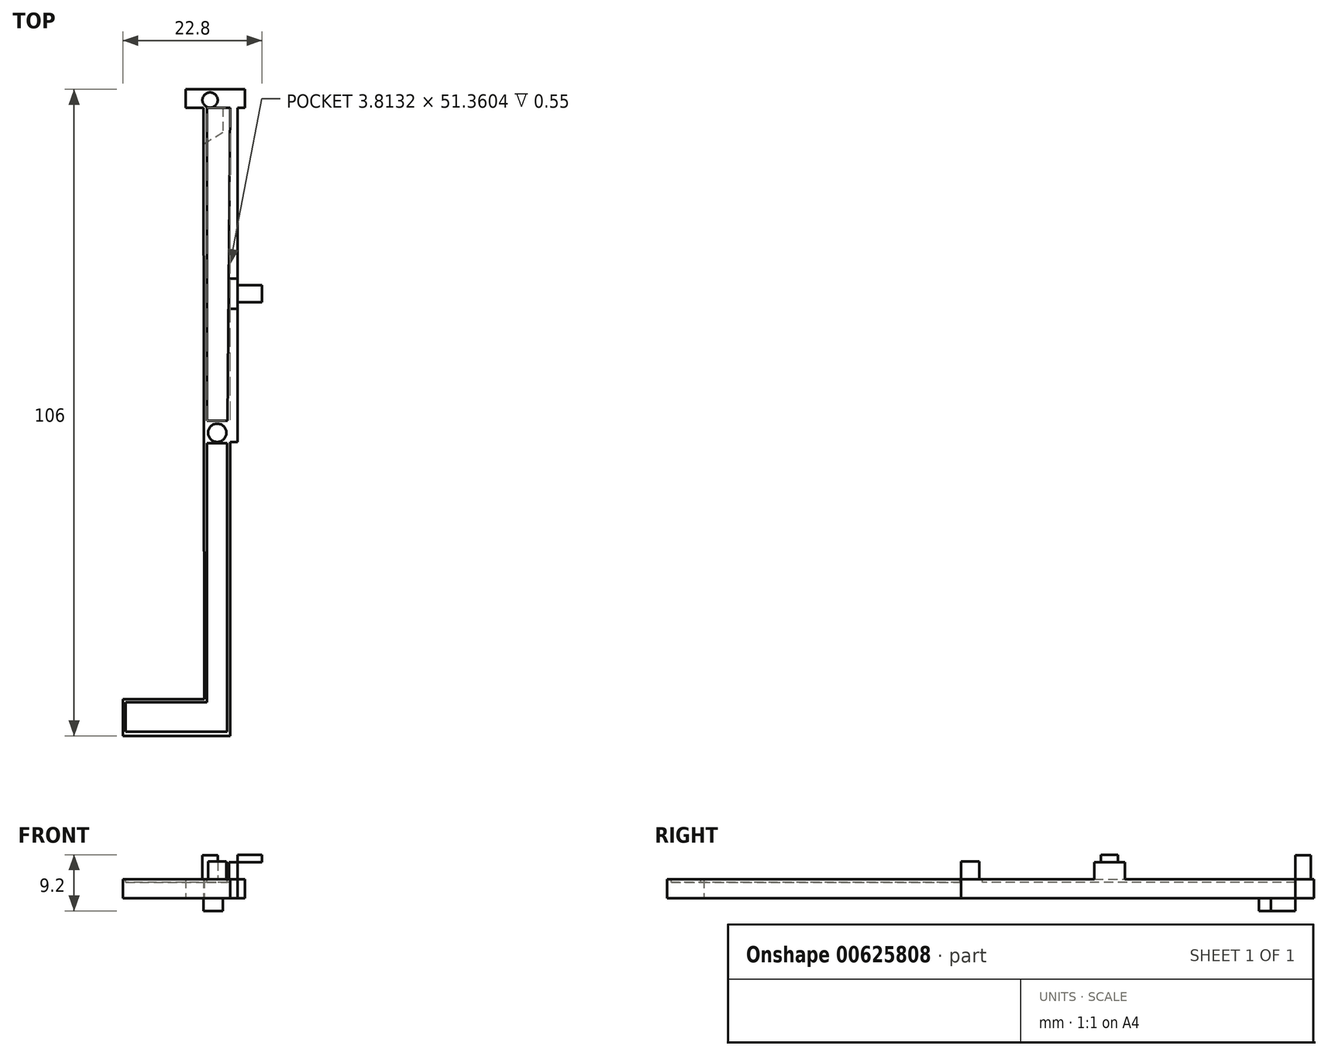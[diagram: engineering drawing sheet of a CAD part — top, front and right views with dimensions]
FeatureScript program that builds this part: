
annotation { "Feature Type Name" : "Feature", "Feature Type Description" : "" }
export const myFeature = defineFeature(function(context is Context, id is Id, definition is map)
    precondition{}
    {
        {
            var Q0;
            Q0=qCreatedBy(makeId("Top.planeOp"),FACE);
            var sketch = newSketch(context, id + "F0", { "sketchPlane" : qUnion([Q0])});
            skLineSegment(sketch, "E0", {"start": v(0, 3) * mm, "end": v(0, 0) * mm});
            skLineSegment(sketch, "E1", {"start": v(0, 0) * mm, "end": v(-1.2, 0) * mm});
            skLineSegment(sketch, "E2", {"start": v(0, 3) * mm, "end": v(-9.7, 3) * mm});
            skLineSegment(sketch, "E3", {"start": v(-9.7, 3) * mm, "end": v(-9.7, 0) * mm});
            skLineSegment(sketch, "E4", {"start": v(-9.7, 0) * mm, "end": v(-6.8, 0) * mm});
            skLineSegment(sketch, "E5", {"start": v(-1.2, 0) * mm, "end": v(-1.2, -54.8) * mm});
            skLineSegment(sketch, "E6", {"start": v(-1.2, -54.8) * mm, "end": v(-2.4, -54.8) * mm});
            skLineSegment(sketch, "E7", {"start": v(-2.4, -54.8) * mm, "end": v(-2.4, -103) * mm});
            skLineSegment(sketch, "E8", {"start": v(-2.4, -103) * mm, "end": v(-20, -103) * mm});
            skLineSegment(sketch, "E9", {"start": v(-20, -103) * mm, "end": v(-20, -97) * mm});
            skLineSegment(sketch, "E10", {"start": v(-20, -97) * mm, "end": v(-6.7, -97) * mm});
            skLineSegment(sketch, "E11", {"start": v(-6.7, -97) * mm, "end": v(-6.8, 0) * mm});
            skSolve(sketch);
        }
        {
            var Q0;
            Q0 = qSketchRegion(id + "F0", true);
            extrude(context, id + "F1", {"entities" : qUnion([Q0]), "depth" : 3.1 * mm, "offsetDistance" : 25 * mm});
        }
        {
            var Q0;
            Q0=makeQuery(id+"F1.opExtrude","CAP_FACE",FACE,{"disambiguationData":[OSD([sQuery(id+"F0.wireOp",EDGE,"E0"),sQuery(id+"F0.wireOp",EDGE,"E1"),sQuery(id+"F0.wireOp",EDGE,"E2"),sQuery(id+"F0.wireOp",EDGE,"E3"),sQuery(id+"F0.wireOp",EDGE,"E4"),sQuery(id+"F0.wireOp",EDGE,"E5"),sQuery(id+"F0.wireOp",EDGE,"E6"),sQuery(id+"F0.wireOp",EDGE,"E7"),sQuery(id+"F0.wireOp",EDGE,"E8"),sQuery(id+"F0.wireOp",EDGE,"E9"),sQuery(id+"F0.wireOp",EDGE,"E10"),sQuery(id+"F0.wireOp",EDGE,"E11")])],"isStart":true});
            var sketch = newSketch(context, id + "F2", { "sketchPlane" : qUnion([Q0])});
            skLineSegment(sketch, "E12", {"start": v(-6.8, 0) * mm, "end": v(-3.62, 0) * mm});
            skLineSegment(sketch, "E13", {"start": v(-3.62, 0) * mm, "end": v(-3.62, 4) * mm});
            skLineSegment(sketch, "E14", {"start": v(-6.8, 0) * mm, "end": v(-6.8, 6) * mm});
            skLineSegment(sketch, "E15", {"start": v(-6.8, 6) * mm, "end": v(-3.62, 4) * mm});
            skSolve(sketch);
        }
        {
            var Q0;
            Q0=makeQuery(id+"F2.imprint","IMPRINT",FACE,{"disambiguationData":[TD([[makeQuery(id+"F2.imprint","IMPRINT",EDGE,{"derivedFrom":sQuery(id+"F2.wireOp",EDGE,"E12")}),1.0]])]});
            extrude(context, id + "F3", {"entities" : qUnion([Q0]), "operationType" : NewBodyOperationType.ADD, "depth" : 2.1 * mm, "offsetDistance" : 25 * mm});
        }
        {
            var Q0;
            Q0=makeQuery(id+"F1.opExtrude","CAP_FACE",FACE,{"disambiguationData":[OSD([sQuery(id+"F0.wireOp",EDGE,"E0"),sQuery(id+"F0.wireOp",EDGE,"E1"),sQuery(id+"F0.wireOp",EDGE,"E2"),sQuery(id+"F0.wireOp",EDGE,"E3"),sQuery(id+"F0.wireOp",EDGE,"E4"),sQuery(id+"F0.wireOp",EDGE,"E5"),sQuery(id+"F0.wireOp",EDGE,"E6"),sQuery(id+"F0.wireOp",EDGE,"E7"),sQuery(id+"F0.wireOp",EDGE,"E8"),sQuery(id+"F0.wireOp",EDGE,"E9"),sQuery(id+"F0.wireOp",EDGE,"E10"),sQuery(id+"F0.wireOp",EDGE,"E11")])],"isStart":false});
            var sketch = newSketch(context, id + "F4", { "sketchPlane" : qUnion([Q0])});
            skCircle(sketch, "E16", {"center": v(-5.71, 1.25) * mm, "radius": 1.25 * mm});
            skSolve(sketch);
        }
        {
            var Q0;
            Q0 = qSketchRegion(id + "F4", true);
            extrude(context, id + "F5", {"entities" : qUnion([Q0]), "operationType" : NewBodyOperationType.ADD, "depth" : 3.9 * mm, "offsetDistance" : 25 * mm});
        }
        {
            var Q0;
            Q0=makeQuery(id+"F1.opExtrude","CAP_FACE",FACE,{"disambiguationData":[OSD([sQuery(id+"F0.wireOp",EDGE,"E0"),sQuery(id+"F0.wireOp",EDGE,"E1"),sQuery(id+"F0.wireOp",EDGE,"E2"),sQuery(id+"F0.wireOp",EDGE,"E3"),sQuery(id+"F0.wireOp",EDGE,"E4"),sQuery(id+"F0.wireOp",EDGE,"E5"),sQuery(id+"F0.wireOp",EDGE,"E6"),sQuery(id+"F0.wireOp",EDGE,"E7"),sQuery(id+"F0.wireOp",EDGE,"E8"),sQuery(id+"F0.wireOp",EDGE,"E9"),sQuery(id+"F0.wireOp",EDGE,"E10"),sQuery(id+"F0.wireOp",EDGE,"E11")])],"isStart":false});
            var sketch = newSketch(context, id + "F6", { "sketchPlane" : qUnion([Q0])});
            skLineSegment(sketch, "E17", {"start": v(-1.2, -33) * mm, "end": v(-1.2, -28) * mm});
            skLineSegment(sketch, "E18", {"start": v(-1.2, -33) * mm, "end": v(-2.6, -33) * mm});
            skLineSegment(sketch, "E19", {"start": v(-2.6, -33) * mm, "end": v(-2.6, -28) * mm});
            skLineSegment(sketch, "E20", {"start": v(-2.6, -28) * mm, "end": v(-1.2, -28) * mm});
            skSolve(sketch);
        }
        {
            var Q0;
            Q0=makeQuery(id+"F6.imprint","IMPRINT",FACE,{"disambiguationData":[TD([[makeQuery(id+"F6.imprint","IMPRINT",EDGE,{"derivedFrom":sQuery(id+"F6.wireOp",EDGE,"E17")}),-1.0]])]});
            extrude(context, id + "F7", {"entities" : qUnion([Q0]), "operationType" : NewBodyOperationType.ADD, "depth" : 2.8 * mm, "offsetDistance" : 25 * mm});
        }
        {
            var Q0;
            Q0=makeQuery(id+"F7.opExtrude","CAP_FACE",FACE,{"disambiguationData":[OSD([sQuery(id+"F6.wireOp",EDGE,"E17"),sQuery(id+"F6.wireOp",EDGE,"E18"),sQuery(id+"F6.wireOp",EDGE,"E19"),sQuery(id+"F6.wireOp",EDGE,"E20")])],"isStart":false});
            var sketch = newSketch(context, id + "F8", { "sketchPlane" : qUnion([Q0])});
            skLineSegment(sketch, "E21", {"start": v(-1.2, -31.9) * mm, "end": v(-1.2, -29.1) * mm});
            skLineSegment(sketch, "E22", {"start": v(-1.2, -31.9) * mm, "end": v(2.8, -31.9) * mm});
            skLineSegment(sketch, "E23", {"start": v(2.8, -31.9) * mm, "end": v(2.8, -29.1) * mm});
            skLineSegment(sketch, "E24", {"start": v(2.8, -29.1) * mm, "end": v(-1.2, -29.1) * mm});
            skSolve(sketch);
        }
        {
            var Q0;
            Q0=makeQuery(id+"F8.imprint","IMPRINT",FACE,{"disambiguationData":[TD([[makeQuery(id+"F8.imprint","IMPRINT",EDGE,{"derivedFrom":sQuery(id+"F8.wireOp",EDGE,"E21")}),1.0]])]});
            extrude(context, id + "F9", {"entities" : qUnion([Q0]), "depth" : 1.2 * mm, "offsetDistance" : 25 * mm});
        }
        {
            var Q0;
            Q0=makeQuery(id+"F1.opExtrude","CAP_FACE",FACE,{"disambiguationData":[OSD([sQuery(id+"F0.wireOp",EDGE,"E0"),sQuery(id+"F0.wireOp",EDGE,"E1"),sQuery(id+"F0.wireOp",EDGE,"E2"),sQuery(id+"F0.wireOp",EDGE,"E3"),sQuery(id+"F0.wireOp",EDGE,"E4"),sQuery(id+"F0.wireOp",EDGE,"E5"),sQuery(id+"F0.wireOp",EDGE,"E6"),sQuery(id+"F0.wireOp",EDGE,"E7"),sQuery(id+"F0.wireOp",EDGE,"E8"),sQuery(id+"F0.wireOp",EDGE,"E9"),sQuery(id+"F0.wireOp",EDGE,"E10"),sQuery(id+"F0.wireOp",EDGE,"E11")])],"isStart":false});
            var sketch = newSketch(context, id + "F10", { "sketchPlane" : qUnion([Q0])});
            skCircle(sketch, "E25", {"center": v(-4.55, -53.32) * mm, "radius": 1.5 * mm});
            skLineSegment(sketch, "E26", {"start": v(-2.4, -54.8) * mm, "end": v(-6.74, -54.83) * mm});
            skSolve(sketch);
        }
        {
            var Q0;
            Q0=makeQuery(id+"F10.imprint","IMPRINT",FACE,{"disambiguationData":[TD([[makeQuery(id+"F10.imprint","IMPRINT",EDGE,{"derivedFrom":sQuery(id+"F10.wireOp",EDGE,"E25")}),1.0]])]});
            extrude(context, id + "F11", {"entities" : qUnion([Q0]), "operationType" : NewBodyOperationType.ADD, "depth" : 2.9 * mm, "offsetDistance" : 25 * mm});
        }
        {
            var Q0;
            Q0=makeQuery(id+"F1.opExtrude","CAP_FACE",FACE,{"disambiguationData":[OSD([sQuery(id+"F0.wireOp",EDGE,"E0"),sQuery(id+"F0.wireOp",EDGE,"E1"),sQuery(id+"F0.wireOp",EDGE,"E2"),sQuery(id+"F0.wireOp",EDGE,"E3"),sQuery(id+"F0.wireOp",EDGE,"E4"),sQuery(id+"F0.wireOp",EDGE,"E5"),sQuery(id+"F0.wireOp",EDGE,"E6"),sQuery(id+"F0.wireOp",EDGE,"E7"),sQuery(id+"F0.wireOp",EDGE,"E8"),sQuery(id+"F0.wireOp",EDGE,"E9"),sQuery(id+"F0.wireOp",EDGE,"E10"),sQuery(id+"F0.wireOp",EDGE,"E11")])],"isStart":false});
            var sketch = newSketch(context, id + "F12", { "sketchPlane" : qUnion([Q0])});
            skPoint(sketch, "E27.endSnap0", {"position": v(-2.4, -78.9) * mm});
            skLineSegment(sketch, "E28", {"start": v(-2.4, 0) * mm, "end": v(-6.21, 0) * mm});
            skLineSegment(sketch, "E29", {"start": v(-6.21, 0) * mm, "end": v(-6.21, -51.33) * mm});
            skLineSegment(sketch, "E30", {"start": v(-6.21, -51.33) * mm, "end": v(-2.85, -51.36) * mm});
            skLineSegment(sketch, "E31", {"start": v(-2.4, 0) * mm, "end": v(-2.85, -51.36) * mm});
            skSolve(sketch);
        }
        {
            var Q0;
            {var subQ6=sQuery(id+"F0.wireOp",EDGE,"E0");Q0=makeQuery(id+"F12.imprint","IMPRINT",FACE,{"disambiguationData":[TD([[makeQuery(id+"F12.imprint","IMPRINT",EDGE,{"derivedFrom":makeQuery(id+"F1.opExtrude","CAP_EDGE",EDGE,{"disambiguationData":[OSD([subQ6])],"isStart":false})}),-1.0]])]});}
            var sketch = newSketch(context, id + "F13", { "sketchPlane" : qUnion([Q0])});
            skLineSegment(sketch, "E32", {"start": v(-2.95, -55) * mm, "end": v(-2.95, -102.33) * mm});
            skLineSegment(sketch, "E33", {"start": v(-2.95, -102.33) * mm, "end": v(-19.53, -102.33) * mm});
            skLineSegment(sketch, "E34", {"start": v(-19.53, -102.33) * mm, "end": v(-19.53, -97.5) * mm});
            skLineSegment(sketch, "E35", {"start": v(-19.53, -97.5) * mm, "end": v(-6.23, -97.5) * mm});
            skLineSegment(sketch, "E36", {"start": v(-6.23, -97.5) * mm, "end": v(-6.23, -55) * mm});
            skLineSegment(sketch, "E37", {"start": v(-6.23, -55) * mm, "end": v(-2.95, -55) * mm});
            skSolve(sketch);
        }
        {
            var Q0;
            Q0=makeQuery(id+"F13.imprint","IMPRINT",FACE,{"disambiguationData":[TD([[makeQuery(id+"F13.imprint","IMPRINT",EDGE,{"derivedFrom":sQuery(id+"F13.wireOp",EDGE,"E32")}),-1.0]])]});
            extrude(context, id + "F14", {"entities" : qUnion([Q0]), "operationType" : NewBodyOperationType.REMOVE, "oppositeDirection" : true, "depth" : 0.55 * mm, "offsetDistance" : 25 * mm});
        }
        {
            var Q0;
            Q0=makeQuery(id+"F12.imprint","IMPRINT",FACE,{"disambiguationData":[TD([[makeQuery(id+"F12.imprint","IMPRINT",EDGE,{"derivedFrom":sQuery(id+"F12.wireOp",EDGE,"E28")}),1.0]])]});
            extrude(context, id + "F15", {"entities" : qUnion([Q0]), "operationType" : NewBodyOperationType.REMOVE, "oppositeDirection" : true, "depth" : 0.55 * mm, "offsetDistance" : 25 * mm});
        }
    });
